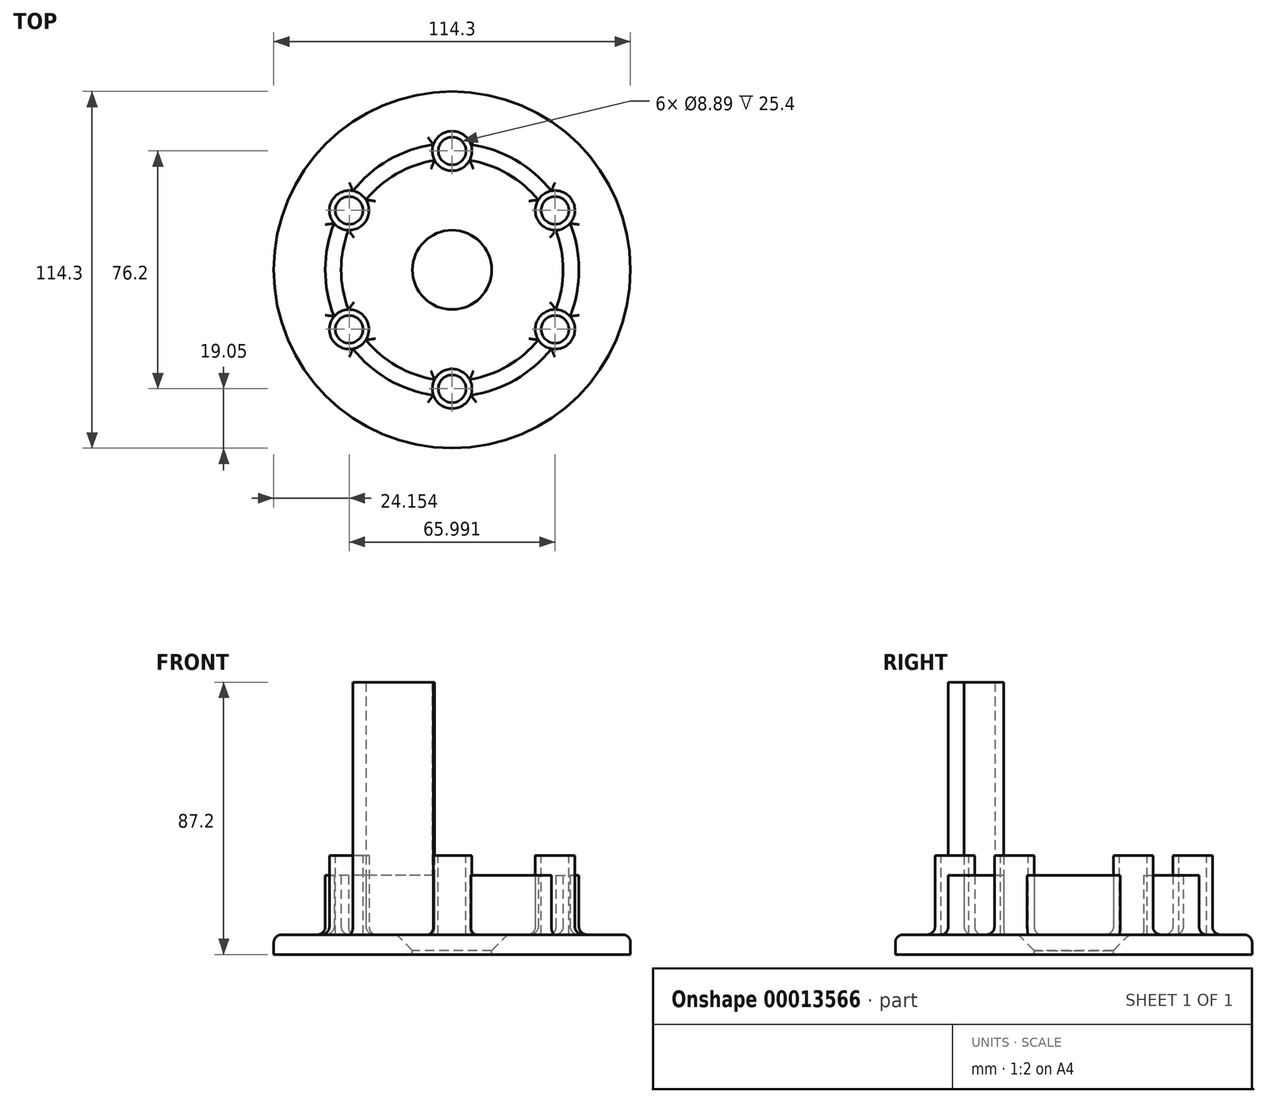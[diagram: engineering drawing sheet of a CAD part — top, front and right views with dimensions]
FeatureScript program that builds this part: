
annotation { "Feature Type Name" : "Feature", "Feature Type Description" : "" }
export const myFeature = defineFeature(function(context is Context, id is Id, definition is map)
    precondition{}
    {
        {
            var Q0;
            Q0=qCreatedBy(makeId("Top.planeOp"),FACE);
            var sketch = newSketch(context, id + "F0", { "sketchPlane" : qUnion([Q0])});
            skCircle(sketch, "E0", {"center": v(0, 0) * mm, "radius": 57.15 * mm});
            skCircle(sketch, "E1", {"center": v(0, 0) * mm, "radius": 38.1 * mm, "construction": true});
            skCircle(sketch, "E2.0", {"center": v(0, 0) * mm, "radius": 44.45 * mm, "construction": true});
            skCircle(sketch, "E3.0", {"center": v(0, 0) * mm, "radius": 31.75 * mm, "construction": true});
            skCircle(sketch, "E4.0", {"center": v(0, 0) * mm, "radius": 40.64 * mm});
            skCircle(sketch, "E5.0", {"center": v(0, 0) * mm, "radius": 35.56 * mm});
            skCircle(sketch, "E6", {"center": v(0, 38.1) * mm, "radius": 6.35 * mm});
            skCircle(sketch, "E7.1.0", {"center": v(-33, 19.05) * mm, "radius": 6.35 * mm});
            skCircle(sketch, "E7.2.0", {"center": v(-33, -19.05) * mm, "radius": 6.35 * mm});
            skCircle(sketch, "E7.3.0", {"center": v(0, -38.1) * mm, "radius": 6.35 * mm});
            skCircle(sketch, "E7.4.0", {"center": v(33, -19.05) * mm, "radius": 6.35 * mm});
            skCircle(sketch, "E7.5.0", {"center": v(33, 19.05) * mm, "radius": 6.35 * mm});
            skCircle(sketch, "E8", {"center": v(0, 0) * mm, "radius": 12.7 * mm});
            skSolve(sketch);
        }
        {
            var Q0;
            Q0=qCreatedBy(makeId("Top.planeOp"),FACE);
            var sketch = newSketch(context, id + "F1", { "sketchPlane" : qUnion([Q0])});
            skCircle(sketch, "E9.0", {"center": v(0, 0) * mm, "radius": 57.15 * mm});
            skCircle(sketch, "E10.0", {"center": v(0, 0) * mm, "radius": 12.7 * mm});
            skSolve(sketch);
        }
        {
            var Q0;
            Q0 = qSketchRegion(id + "F1", true);
            extrude(context, id + "F2", {"entities" : qUnion([Q0]), "oppositeDirection" : true, "depth" : 6.35 * mm});
        }
        {
            var Q0;
            Q0=makeQuery(id+"F0.imprint","IMPRINT",FACE,{"disambiguationData":[TD([[makeQuery(id+"F0.imprint","IMPRINT",EDGE,{"derivedFrom":sQuery(id+"F0.wireOp",EDGE,"E0")}),1.0]])]});
            var sketch = newSketch(context, id + "F3", { "sketchPlane" : qUnion([Q0])});
            skCircle(sketch, "E11.0", {"center": v(0, -38.1) * mm, "radius": 6.35 * mm});
            skCircle(sketch, "E12.0", {"center": v(-33, -19.05) * mm, "radius": 6.35 * mm});
            skCircle(sketch, "E13.0", {"center": v(-33, 19.05) * mm, "radius": 6.35 * mm});
            skCircle(sketch, "E14.0", {"center": v(0, 38.1) * mm, "radius": 6.35 * mm});
            skCircle(sketch, "E15.0", {"center": v(33, 19.05) * mm, "radius": 6.35 * mm});
            skCircle(sketch, "E16.0", {"center": v(33, -19.05) * mm, "radius": 6.35 * mm});
            skSolve(sketch);
        }
        {
            var Q0;
            Q0 = qSketchRegion(id + "F3", true);
            extrude(context, id + "F4", {"entities" : qUnion([Q0]), "operationType" : NewBodyOperationType.ADD, "depth" : 25.4 * mm});
        }
        {
            var Q0;
            Q0=makeQuery(id+"F0.imprint","IMPRINT",FACE,{"disambiguationData":[TD([[makeQuery(id+"F0.imprint","IMPRINT",EDGE,{"derivedFrom":sQuery(id+"F0.wireOp",EDGE,"E0")}),1.0]])]});
            var sketch = newSketch(context, id + "F5", { "sketchPlane" : qUnion([Q0])});
            skCircle(sketch, "E17.0", {"center": v(0, 0) * mm, "radius": 40.64 * mm});
            skCircle(sketch, "E18.0", {"center": v(0, 0) * mm, "radius": 35.56 * mm});
            skSolve(sketch);
        }
        {
            var Q0;
            Q0 = qSketchRegion(id + "F5", true);
            extrude(context, id + "F6", {"entities" : qUnion([Q0]), "operationType" : NewBodyOperationType.ADD, "depth" : 19.05 * mm});
        }
        {
            var Q0;
            Q0=makeQuery(id+"F4.opExtrude","CAP_FACE",FACE,{"disambiguationData":[OSD([sQuery(id+"F3.wireOp",EDGE,"E14.0")])],"isStart":false});
            var sketch = newSketch(context, id + "F7", { "sketchPlane" : qUnion([Q0])});
            skPoint(sketch, "E19.0", {"position": v(0, 38.1) * mm});
            skCircle(sketch, "E20", {"center": v(0, 38.1) * mm, "radius": 4.45 * mm});
            skCircle(sketch, "E21.1.0", {"center": v(-33, 19.05) * mm, "radius": 4.45 * mm});
            skCircle(sketch, "E21.2.0", {"center": v(-33, -19.05) * mm, "radius": 4.45 * mm});
            skCircle(sketch, "E21.3.0", {"center": v(0, -38.1) * mm, "radius": 4.45 * mm});
            skCircle(sketch, "E21.4.0", {"center": v(33, -19.05) * mm, "radius": 4.45 * mm});
            skCircle(sketch, "E21.5.0", {"center": v(33, 19.05) * mm, "radius": 4.45 * mm});
            skPoint(sketch, "E21.center", {"position": v(0, 0) * mm});
            skSolve(sketch);
        }
        {
            var Q0;
            Q0 = qSketchRegion(id + "F7", true);
            extrude(context, id + "F8", {"entities" : qUnion([Q0]), "operationType" : NewBodyOperationType.REMOVE, "oppositeDirection" : true, "depth" : 25.4 * mm});
        }
        {
            var Q0;
            Q0=makeQuery(id+"F2.opExtrude","CAP_EDGE",EDGE,{"disambiguationData":[OSD([sQuery(id+"F1.wireOp",EDGE,"E10.0")])],"isStart":true});
            chamfer(context, id + "F9", {"entities" : qUnion([Q0]), "width" : 5.08 * mm, "tangentPropagation" : true});
        }
        {
            var Q0;
            {var subQ0=sQuery(id+"F5.wireOp",EDGE,"E17.0");Q0=makeQuery(id+"F6.boolean.opBoolean","SPLIT",EDGE,{"disambiguationData":[TD([makeQuery(id+"F2.opExtrude","CAP_FACE",FACE,{"disambiguationData":[OSD([sQuery(id+"F1.wireOp",EDGE,"E9.0"),sQuery(id+"F1.wireOp",EDGE,"E10.0")])],"isStart":true}),makeQuery(id+"F4.opExtrude","SWEPT_FACE",FACE,{"disambiguationData":[OSD([sQuery(id+"F3.wireOp",EDGE,"E11.0")])]}),makeQuery(id+"F4.opExtrude","SWEPT_FACE",FACE,{"disambiguationData":[OSD([sQuery(id+"F3.wireOp",EDGE,"E12.0")])]}),makeQuery(id+"F6.opExtrude","SWEPT_FACE",FACE,{"disambiguationData":[OSD([subQ0])]})])],"derivedFrom":makeQuery(id+"F6.opExtrude","CAP_EDGE",EDGE,{"disambiguationData":[OSD([subQ0])],"isStart":true})});}
            var Q1;
            {var subQ0=sQuery(id+"F5.wireOp",EDGE,"E17.0");Q1=makeQuery(id+"F6.boolean.opBoolean","SPLIT",EDGE,{"disambiguationData":[TD([makeQuery(id+"F2.opExtrude","CAP_FACE",FACE,{"disambiguationData":[OSD([sQuery(id+"F1.wireOp",EDGE,"E9.0"),sQuery(id+"F1.wireOp",EDGE,"E10.0")])],"isStart":true}),makeQuery(id+"F4.opExtrude","SWEPT_FACE",FACE,{"disambiguationData":[OSD([sQuery(id+"F3.wireOp",EDGE,"E11.0")])]}),makeQuery(id+"F4.opExtrude","SWEPT_FACE",FACE,{"disambiguationData":[OSD([sQuery(id+"F3.wireOp",EDGE,"E16.0")])]}),makeQuery(id+"F6.opExtrude","SWEPT_FACE",FACE,{"disambiguationData":[OSD([subQ0])]})])],"derivedFrom":makeQuery(id+"F6.opExtrude","CAP_EDGE",EDGE,{"disambiguationData":[OSD([subQ0])],"isStart":true})});}
            var Q2;
            {var subQ0=sQuery(id+"F1.wireOp",EDGE,"E9.0");Q2=makeQuery(id+"F6.boolean.opBoolean","SPLIT",FACE,{"disambiguationData":[TD([makeQuery(id+"F2.opExtrude","SWEPT_FACE",FACE,{"disambiguationData":[OSD([subQ0])]})])],"derivedFrom":makeQuery(id+"F2.opExtrude","CAP_FACE",FACE,{"disambiguationData":[OSD([subQ0,sQuery(id+"F1.wireOp",EDGE,"E10.0")])],"isStart":true})});}
            var Q3;
            {var subQ0=sQuery(id+"F1.wireOp",EDGE,"E10.0");Q3=makeQuery(id+"F6.boolean.opBoolean","SPLIT",FACE,{"disambiguationData":[TD([makeQuery(id+"F2.opExtrude","SWEPT_FACE",FACE,{"disambiguationData":[OSD([subQ0])]})])],"derivedFrom":makeQuery(id+"F2.opExtrude","CAP_FACE",FACE,{"disambiguationData":[OSD([sQuery(id+"F1.wireOp",EDGE,"E9.0"),subQ0])],"isStart":true})});}
            fillet(context, id + "F10", {"entities" : qUnion([Q0, Q1, Q2, Q3]), "radius" : 2.54 * mm, "tangentPropagation" : true, "allowEdgeOverflow" : false});
        }
        {
            var Q0;
            {var subQ0=sQuery(id+"F5.wireOp",EDGE,"E17.0");var subQ1=sQuery(id+"F5.wireOp",EDGE,"E18.0");Q0=makeQuery(id+"F6.boolean.opBoolean","SPLIT",FACE,{"disambiguationData":[TD([makeQuery(id+"F4.opExtrude","SWEPT_FACE",FACE,{"disambiguationData":[OSD([sQuery(id+"F3.wireOp",EDGE,"E11.0")])]}),makeQuery(id+"F4.opExtrude","SWEPT_FACE",FACE,{"disambiguationData":[OSD([sQuery(id+"F3.wireOp",EDGE,"E12.0")])]}),makeQuery(id+"F6.opExtrude","SWEPT_FACE",FACE,{"disambiguationData":[OSD([subQ0])]}),makeQuery(id+"F6.opExtrude","SWEPT_FACE",FACE,{"disambiguationData":[OSD([subQ1])]})])],"derivedFrom":makeQuery(id+"F6.opExtrude","CAP_FACE",FACE,{"disambiguationData":[OSD([subQ0,subQ1])],"isStart":false})});}
            extrude(context, id + "F11", {"entities" : qUnion([Q0]), "operationType" : NewBodyOperationType.ADD, "depth" : 61.8 * mm});
        }
    });
